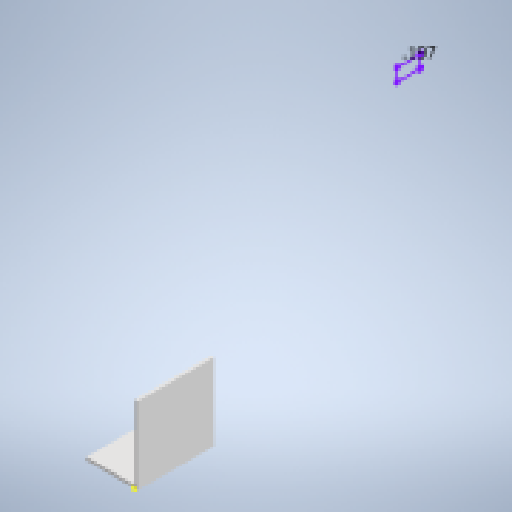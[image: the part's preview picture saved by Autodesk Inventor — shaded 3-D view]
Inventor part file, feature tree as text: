
AUTODESK INVENTOR PART (.ipt)
format: ipt  version: 2023 (Build 270158000, 158)  size: 156,672 bytes
history: native  units: in
note: dims shown in document units (in); Inventor stores cm internally (conversion verified against a paired STEP export)
features: extrude x2, sketch x2, shell x1
ambient origin geometry x8: Origin, YZ Plane, XZ Plane, XY Plane, X Axis, Y Axis, Z Axis, Center Point
bodies: Solid1 (feature_tree)
feature tree (5):
  extrude  "Extrusion1"  Depth=3.0in
  shell  "Shell1"  Thickness=3.0in
  extrude  "Extrusion2"  Depth=0.125in
  sketch  "Sketch1"  dims[d0=2.0in d1=3.0in d2=3.0in d3=0.0in]
  sketch  "Sketch2"  dims[d4=0.125in d5=0.1969in d6=1.811in d7=0.5118in d8=1.6112in d9=1.0in d10=0.0in]
